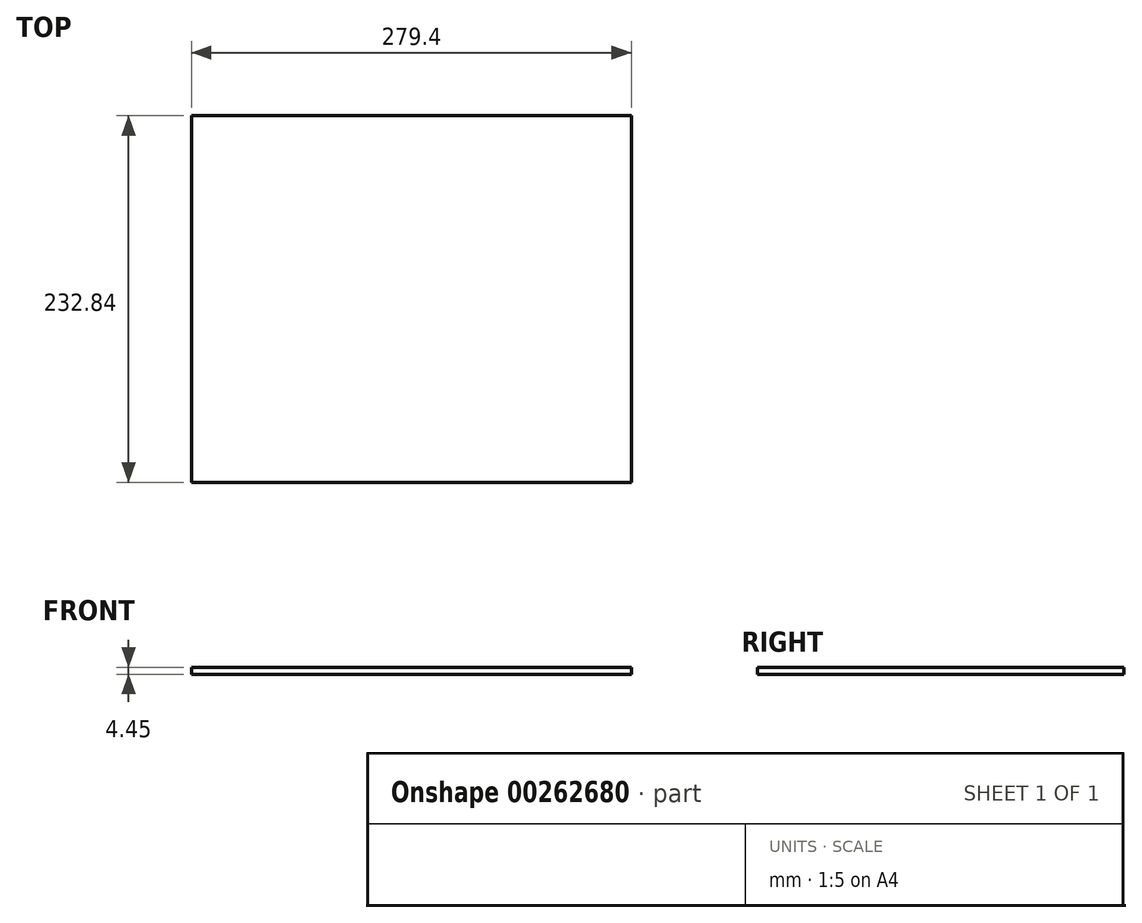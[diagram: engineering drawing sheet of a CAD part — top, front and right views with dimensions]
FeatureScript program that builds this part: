
annotation { "Feature Type Name" : "Feature", "Feature Type Description" : "" }
export const myFeature = defineFeature(function(context is Context, id is Id, definition is map)
    precondition{}
    {
        {
            var Q0;
            Q0=qCreatedBy(makeId("Top.planeOp"),FACE);
            var sketch = newSketch(context, id + "F0", { "sketchPlane" : qUnion([Q0])});
            skLineSegment(sketch, "E0.bottom", {"start": v(0, 0) * mm, "end": v(279.4, 0) * mm});
            skLineSegment(sketch, "E0.top", {"start": v(0, 232.84) * mm, "end": v(279.4, 232.84) * mm});
            skLineSegment(sketch, "E0.left", {"start": v(0, 0) * mm, "end": v(0, 232.84) * mm});
            skLineSegment(sketch, "E0.right", {"start": v(279.4, 0) * mm, "end": v(279.4, 232.84) * mm});
            skSolve(sketch);
        }
        {
            var Q0;
            Q0=makeQuery(id+"F0.imprint","IMPRINT",FACE,{"disambiguationData":[TD([[makeQuery(id+"F0.imprint","IMPRINT",EDGE,{"derivedFrom":sQuery(id+"F0.wireOp",EDGE,"E0.bottom")}),1.0]])]});
            extrude(context, id + "F1", {"entities" : qUnion([Q0]), "depth" : 4.44 * mm});
        }
    });
